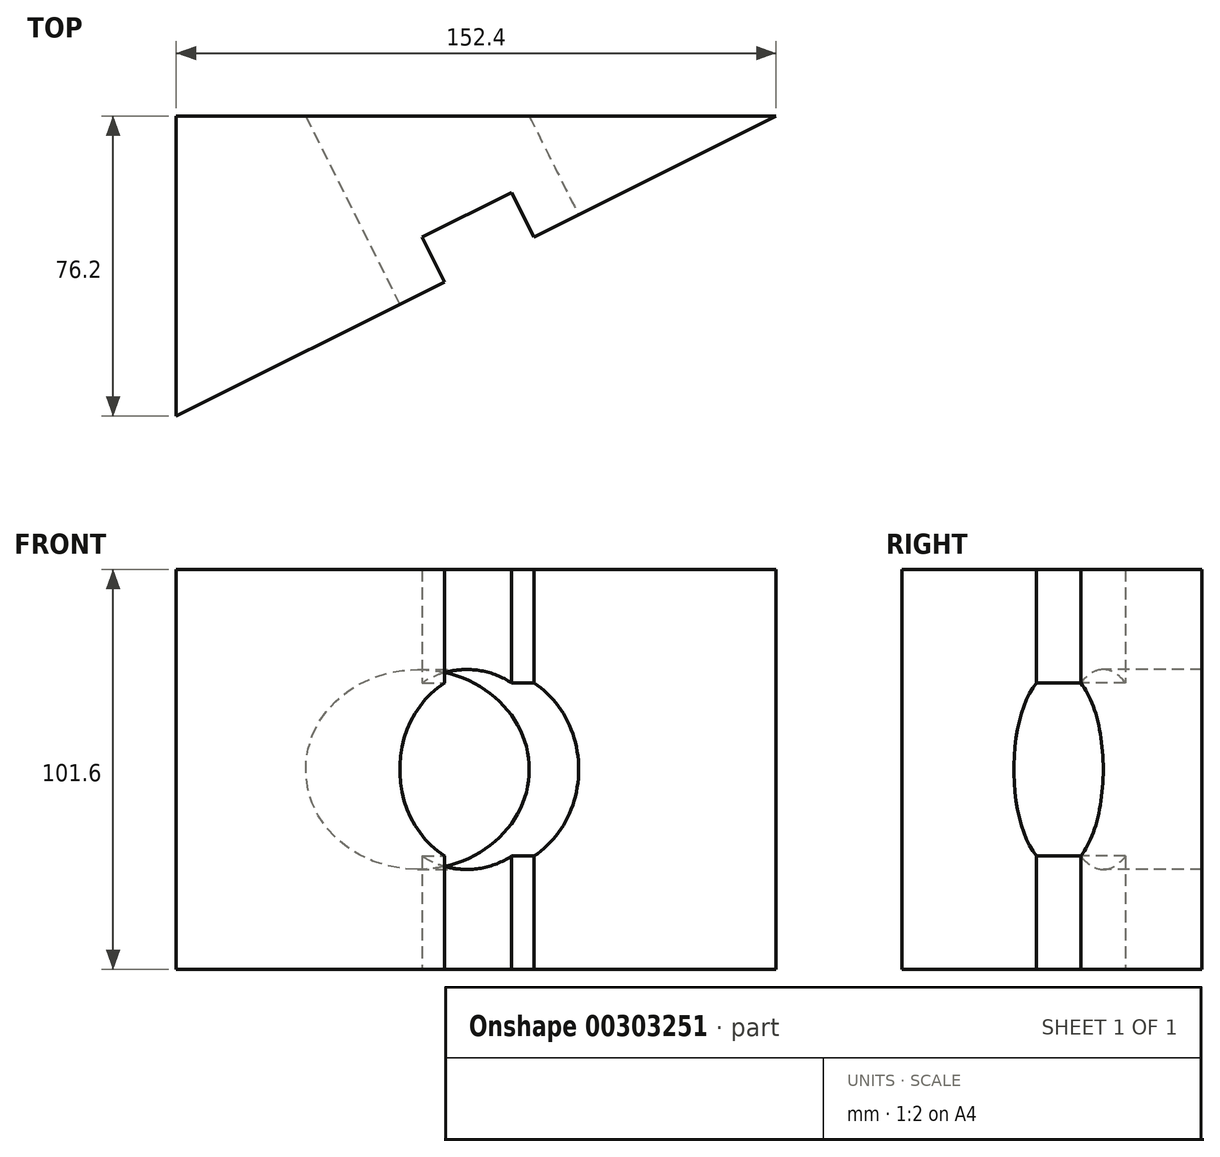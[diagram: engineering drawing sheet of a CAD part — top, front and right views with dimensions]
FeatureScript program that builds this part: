
annotation { "Feature Type Name" : "Feature", "Feature Type Description" : "" }
export const myFeature = defineFeature(function(context is Context, id is Id, definition is map)
    precondition{}
    {
        {
            var Q0;
            Q0=qCreatedBy(makeId("Top.planeOp"),FACE);
            var sketch = newSketch(context, id + "F0", { "sketchPlane" : qUnion([Q0])});
            skLineSegment(sketch, "E0.bottom", {"start": v(0, 0) * mm, "end": v(152.4, 0) * mm});
            skLineSegment(sketch, "E0.top", {"start": v(0, 76.2) * mm, "end": v(152.4, 76.2) * mm});
            skLineSegment(sketch, "E0.left", {"start": v(0, 0) * mm, "end": v(0, 76.2) * mm});
            skLineSegment(sketch, "E0.right", {"start": v(152.4, 0) * mm, "end": v(152.4, 76.2) * mm});
            skLineSegment(sketch, "E1", {"start": v(0, 0) * mm, "end": v(152.4, 76.2) * mm});
            skSolve(sketch);
        }
        {
            var Q0;
            Q0=makeQuery(id+"F0.imprint","IMPRINT",FACE,{"disambiguationData":[TD([[makeQuery(id+"F0.imprint","IMPRINT",EDGE,{"derivedFrom":sQuery(id+"F0.wireOp",EDGE,"E0.top")}),-1.0]])]});
            extrude(context, id + "F1", {"entities" : qUnion([Q0]), "depth" : 101.6 * mm});
        }
        {
            var Q0;
            Q0=makeQuery(id+"F1.opExtrude","SWEPT_FACE",FACE,{"disambiguationData":[OSD([sQuery(id+"F0.wireOp",EDGE,"E1")])]});
            var sketch = newSketch(context, id + "F2", { "sketchPlane" : qUnion([Q0])});
            skLineSegment(sketch, "E2.bottom", {"start": v(101.6, 101.6) * mm, "end": v(76.2, 101.6) * mm});
            skLineSegment(sketch, "E2.top", {"start": v(101.6, 0) * mm, "end": v(76.2, 0) * mm});
            skLineSegment(sketch, "E2.left", {"start": v(101.6, 101.6) * mm, "end": v(101.6, 0) * mm});
            skLineSegment(sketch, "E2.right", {"start": v(76.2, 101.6) * mm, "end": v(76.2, 0) * mm});
            skPoint(sketch, "E2.middle", {"position": v(88.9, 50.8) * mm});
            skSolve(sketch);
        }
        {
            var Q0;
            Q0=makeQuery(id+"F2.imprint","IMPRINT",FACE,{"disambiguationData":[TD([[makeQuery(id+"F2.imprint","IMPRINT",EDGE,{"derivedFrom":sQuery(id+"F2.wireOp",EDGE,"E2.bottom")}),-1.0]])]});
            extrude(context, id + "F3", {"entities" : qUnion([Q0]), "operationType" : NewBodyOperationType.REMOVE, "oppositeDirection" : true, "depth" : 12.7 * mm});
        }
        {
            var Q0;
            {var subQ0=sQuery(id+"F0.wireOp",EDGE,"E1");var subQ1=sQuery(id+"F0.wireOp",EDGE,"E0.left");Q0=makeQuery(id+"F3.boolean.opBoolean","SPLIT",FACE,{"disambiguationData":[TD([makeQuery(id+"F1.opExtrude","SWEPT_FACE",FACE,{"disambiguationData":[OSD([subQ1])]})])],"derivedFrom":makeQuery(id+"F1.opExtrude","SWEPT_FACE",FACE,{"disambiguationData":[OSD([subQ0])]})});}
            var sketch = newSketch(context, id + "F4", { "sketchPlane" : qUnion([Q0])});
            skCircle(sketch, "E3", {"center": v(88.9, 50.8) * mm, "radius": 25.4 * mm});
            skSolve(sketch);
        }
        {
            var Q0;
            Q0 = qSketchRegion(id + "F4", true);
            extrude(context, id + "F5", {"entities" : qUnion([Q0]), "operationType" : NewBodyOperationType.REMOVE, "endBound" : BoundingType.THROUGH_ALL, "oppositeDirection" : true, "depth" : 24.13 * mm});
        }
    });
